# Revit family: Pump_Heavy_Duty-Solid_Handling-Zoeller-X62_HD_Horizontal_Series
name_source: partatom
category: Mechanical Equipment
units: mm (PartAtom-declared; Revit-internal decimal feet)

## family parameters
Always vertical = No
Cut with Voids When Loaded = No
OmniClass Number = 23.60.30.21
OmniClass Title = Pumps
Part Type = Normal
Room Calculation Point = No
Round Connector Dimension = Use Radius
Shared = Yes
Work Plane-Based = Yes

## types (22) — shared parameters
1 Flex Dimension = 10 3/32"
2 Flex Dimesnion = 12 1/2"
4" Flange Horizontal = Yes
6" Flange Horizontal = No
Assembly Code = D2090
Connection Description = 4in Flange Discharge Connection
Cord Length = 300"
Cord Length (Optional) = 600"
Default Elevation = 0"
Description = Solid Handling Pump With Explosion Proof Motor, For Hazardous Location
Discharge Diameter = 4"
Discharge Radius = 2"
Flange = ANSI B16.1
Flange Length = 4 1/2"
Height = 38 3/16"
Hertz = 60
Impeller Type = Ductile Iron Semi-Open
Impeller Type (Optional) Bronze Semi-open = No
Impeller Type (Optional) Ductile Iron Vortex = No
Installation Type = Floor Mounted
Insulation = Class F
Inverted Duty Submersible = No
Length = 18 3/8"
Manufacturer = Zoeller
Material = Cast-Iron-Zoeller-Powder Coated Epoxy
Max. Stator Temp. = 311 °F
Max. Water Temp. = 104 °F
Mechanical Seals = Tandem carbon/ceramic upper and silicon carbide/silicon carbide lower
Min. Recommended Fluid Level = 24"
Moisture Detection = Moisture Sensing Probes
Motor Design Letter = NEMA B
Motor Shaft = 416 S.S.
Motor Thermal Shutoff = Thermal Sensors With Automatic Reset
Motor Type = Explosion Proof Submersible
O-Rings = Buna-N
O-Rings (Optional) Viton = No
Operation = Non-Automatic
Power Cord = <20 = #12-4 SO (Models with a FLA greater than 36.7 amps use #8-4 gauge power cord; #4-4 for less than 36.7)
Price = Prices may vary. Please consult Manufacturer Representative for most up-to-date price list.
Product Documentation Link = http://cdn.qleapahead.com
Product Page URL = http://www.zoellerengprod.com
RPM = 1750
Revised Date = 06/20/2017
Sensor Cord Size = #18-5
Shaft Seal (Standard) = Carbon/Ceramic
Shaft Seal Lower (Options) = Carbon/Silicon Carbide, Silicon Carbide/Silicon Carbide
Shaft Seal Upper (Options) = Carbon/Silicon Carbide, Silicon Carbide/Silicon Carbide
Shipping Weight = 420 lbs. (191 kg)
Solid Size = 3in (75 mm)
Tandem Seals = Standard
URL = http://www.zoellerengprod.com
Warranty Information = 36 Months (Limited)
Waste Connection = Yes
Width = 14 3/4"

## per-type parameters (varying)
| type | Amps | Apparent Load | Flow 6220 @ 5', 6221-6224 @ 10' | Impeller Diameter | Locked Rotor Amps (Voltage Dependant) | Maximum Head | Maximum KW Input | Model | Motor | NEC Locked Rotor Code | Phase | Service Factor | Voltage |
| X6220-230V/1Ph/27.5A/5HP | 28 A | 6325 VA | 785 GPM | 6 7/8" | 91 | 47' | 5.2 | X6220 | 5.0 BHP | D | 1 | 1.2 | 230 V |
| X6220-200V/3Ph/17.5A/5HP | 18 A | 3500 VA | 785 GPM | 6 7/8" | 61.9 | 47' | 5.2 | X6220 | 5.0 BHP | D | 3 | 1.2 | 200 V |
| X6220-230V/3Ph/15.2A/5HP | 15 A | 3496 VA | 785 GPM | 6 7/8" | 53.8 | 47' | 5.2 | X6220 | 5.0 BHP | D | 3 | 1.2 | 230 V |
| X6220-460V/3Ph/7.6A/5HP | 8 A | 3496 VA | 785 GPM | 6 7/8" | 26.9 | 47' | 5.2 | X6220 | 5.0 BHP | D | 3 | 1.2 | 460 V |
| X6220-575V/3Ph/6.1A/5HP | 6 A | 3508 VA | 785 GPM | 6 7/8" | 21.8 | 47' | 5.2 | X6220 | 5.0 BHP | D | 3 | 1.2 | 575 V |
| X6221-230V/1Ph/36.7A/7.5HP | 37 A | 8441 VA | 860 GPM | 7 3/8" | 137 | 57' | 7.8 | X6221 | 7.5 BHP | F | 1 | 1.2 | 230 V |
| X6221-200V/3Ph/25.0A/7.5HP | 25 A | 5000 VA | 860 GPM | 7 3/8" | 109 | 57' | 7.8 | X6221 | 7.5 BHP | F | 3 | 1.2 | 200 V |
| X6221-230V/3Ph/22.0A/7.5HP | 22 A | 5060 VA | 860 GPM | 7 3/8" | 95 | 57' | 7.8 | X6221 | 7.5 BHP | F | 3 | 1.2 | 230 V |
| X6221-460V/3Ph/11.0A/7.5HP | 11 A | 5060 VA | 860 GPM | 7 3/8" | 47.5 | 57' | 7.8 | X6221 | 7.5 BHP | F | 3 | 1.2 | 460 V |
| X6221-575V/3Ph/9.0A/7.5HP | 9 A | 5175 VA | 860 GPM | 7 3/8" | 37.8 | 57' | 7.8 | X6221 | 7.5 BHP | F | 3 | 1.2 | 575 V |
| X6222-200V/3Ph/32.0A/10HP | 32 A | 6400 VA | 960 GPM | 7 3/4" | 109 | 64' | 9.8 | X6222 | 10 BHP | C | 3 | 1.2 | 200 V |
| X6222-230V/3Ph/28.0A/10HP | 28 A | 6440 VA | 960 GPM | 7 3/4" | 95 | 64' | 9.8 | X6222 | 10 BHP | C | 3 | 1.2 | 230 V |
| X6222-460V/3Ph/14.0A/10HP | 14 A | 6440 VA | 960 GPM | 7 3/4" | 47.5 | 64' | 9.8 | X6222 | 10 BHP | C | 3 | 1.2 | 460 V |
| X6222-575V/3Ph/11.0A/10HP | 11 A | 6325 VA | 960 GPM | 7 3/4" | 37.8 | 64' | 9.8 | X6222 | 10 BHP | C | 3 | 1.2 | 575 V |
| X6223-200V/3Ph/48.3A/15HP | 48 A | 9660 VA | 1110 GPM | 8 5/8" | 197 | 81' | 13.5 | X6223 | 15 BHP | E | 3 | 1.2 | 200 V |
| X6223-230V/3Ph/41.7A/15HP | 42 A | 9591 VA | 1110 GPM | 8 5/8" | 172 | 81' | 13.5 | X6223 | 15 BHP | E | 3 | 1.2 | 230 V |
| X6223-460V/3Ph/20.9A/15HP | 21 A | 9614 VA | 1110 GPM | 8 5/8" | 86.0 | 81' | 13.5 | X6223 | 15 BHP | E | 3 | 1.2 | 460 V |
| X6223-575V/3Ph/16.4A/15HP | 16 A | 9430 VA | 1110 GPM | 8 5/8" | 70 | 81' | 13.5 | X6223 | 15 BHP | E | 3 | 1.2 | 575 V |
| X6224-200V/3Ph/59.4A/20HP | 59 A | 11880 VA | 1150 GPM | 9 1/2" | 197 | 100' | 16.8 | X6224 | 20 BHP | B | 3 | 1.0 | 200 V |
| X6224-230V/3Ph/54.0A/20HP | 54 A | 12420 VA | 1150 GPM | 9 1/2" | 172 | 100' | 16.8 | X6224 | 20 BHP | B | 3 | 1.0 | 230 V |
| X6224-460V/3Ph/27.0A/20HP | 27 A | 12420 VA | 1150 GPM | 9 1/2" | 86 | 100' | 16.8 | X6224 | 20 BHP | B | 3 | 1.0 | 460 V |
| X6224-575V/3Ph/22.0A/20HP | 22 A | 12650 VA | 1150 GPM | 9 1/2" | 70 | 100' | 16.8 | X6224 | 20 BHP | B | 3 | 1.0 | 575 V |

## geometry (parser evidence)
native form markers: Sweep x3
no freeform markers — native parametric forms only
